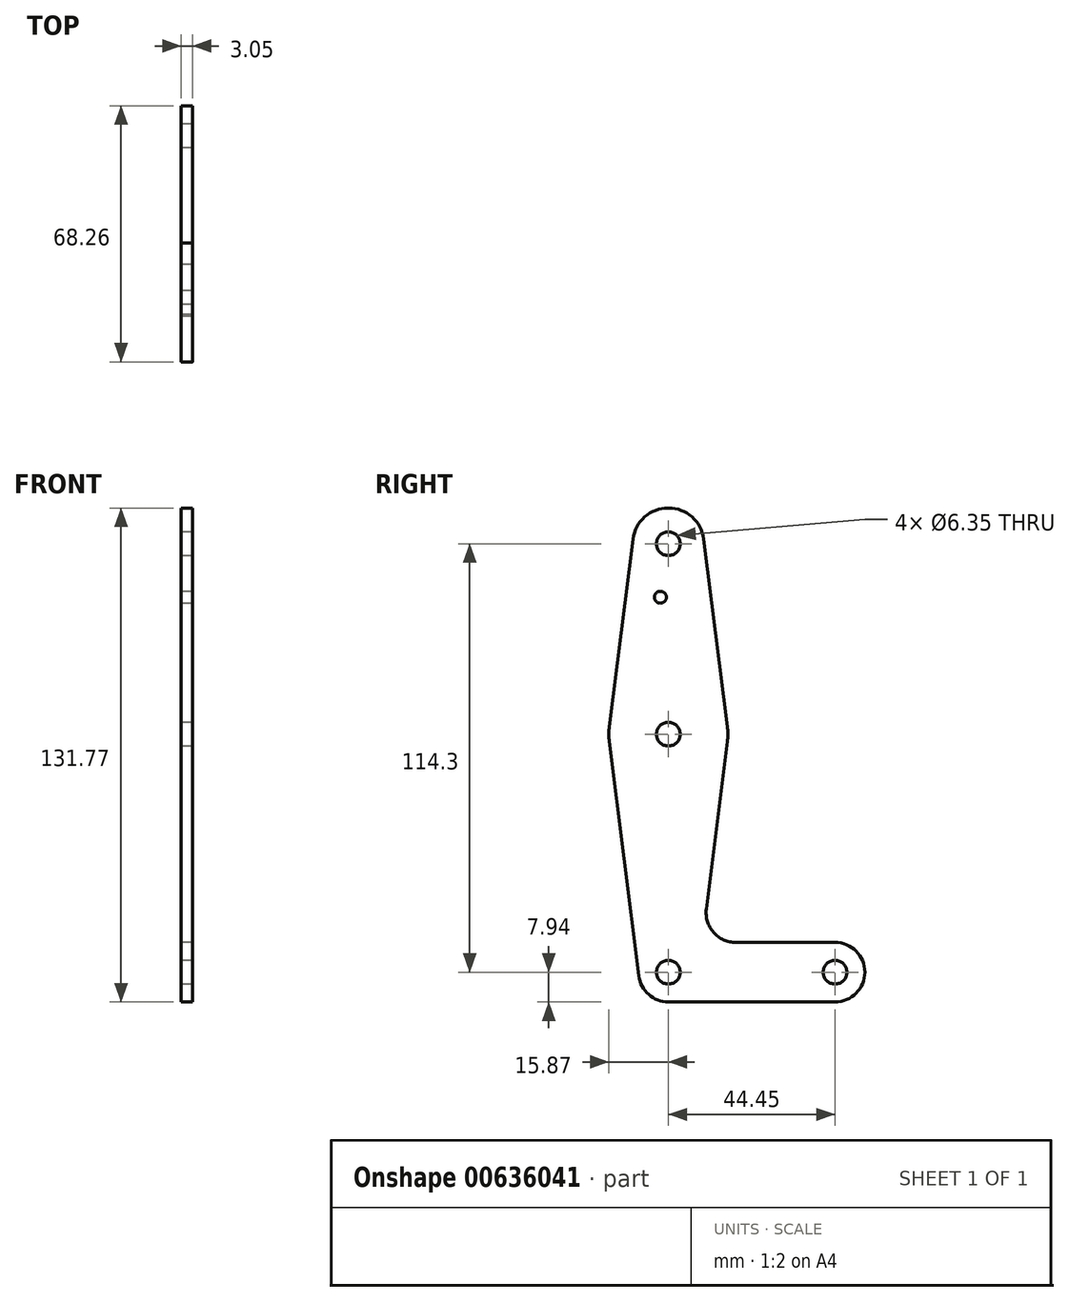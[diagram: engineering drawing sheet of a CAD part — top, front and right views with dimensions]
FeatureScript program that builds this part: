
annotation { "Feature Type Name" : "Feature", "Feature Type Description" : "" }
export const myFeature = defineFeature(function(context is Context, id is Id, definition is map)
    precondition{}
    {
        {
            var Q0;
            Q0=qCreatedBy(makeId("Right.planeOp"),FACE);
            var sketch = newSketch(context, id + "F0", { "sketchPlane" : qUnion([Q0])});
            skCircle(sketch, "E0", {"center": v(0, 0) * mm, "radius": 7.94 * mm});
            skCircle(sketch, "E1", {"center": v(0, 63.5) * mm, "radius": 15.88 * mm});
            skCircle(sketch, "E2", {"center": v(0, 114.3) * mm, "radius": 3.18 * mm});
            skCircle(sketch, "E3", {"center": v(44.45, 0) * mm, "radius": 7.94 * mm});
            skCircle(sketch, "E4", {"center": v(0, 114.3) * mm, "radius": 9.53 * mm});
            skLineSegment(sketch, "E5", {"start": v(0, 0) * mm, "end": v(0, 114.3) * mm, "construction": true});
            skLineSegment(sketch, "E6", {"start": v(0, 0) * mm, "end": v(44.45, 0) * mm, "construction": true});
            skCircle(sketch, "E7", {"center": v(0, 0) * mm, "radius": 3.18 * mm});
            skCircle(sketch, "E8", {"center": v(44.45, 0) * mm, "radius": 3.18 * mm});
            skCircle(sketch, "E9", {"center": v(-2.11, 100.03) * mm, "radius": 1.59 * mm});
            skLineSegment(sketch, "E10", {"start": v(9.45, 115.5) * mm, "end": v(15.75, 65.48) * mm});
            skLineSegment(sketch, "E11", {"start": v(-9.45, 115.5) * mm, "end": v(-15.75, 65.48) * mm});
            skLineSegment(sketch, "E12", {"start": v(-15.75, 61.52) * mm, "end": v(-7.88, -1) * mm});
            skLineSegment(sketch, "E13", {"start": v(0, -7.94) * mm, "end": v(44.45, -7.94) * mm});
            skLineSegment(sketch, "E14", {"start": v(15.75, 61.52) * mm, "end": v(10.13, 16.88) * mm});
            skLineSegment(sketch, "E15", {"start": v(18.01, 7.94) * mm, "end": v(44.45, 7.94) * mm});
            skArc(sketch, "E16.filletArc", {"start": v(10.13, 16.88) * mm, "mid": v(12.05, 10.63) * mm, "end": v(18.01, 7.94) * mm});
            skCircle(sketch, "E17", {"center": v(0, 63.5) * mm, "radius": 3.18 * mm});
            skSolve(sketch);
        }
        {
            var Q0;
            Q0 = qSketchRegion(id + "F0", true);
            extrude(context, id + "F1", {"entities" : qUnion([Q0]), "depth" : 3.05 * mm, "offsetDistance" : 25.4 * mm});
        }
    });
